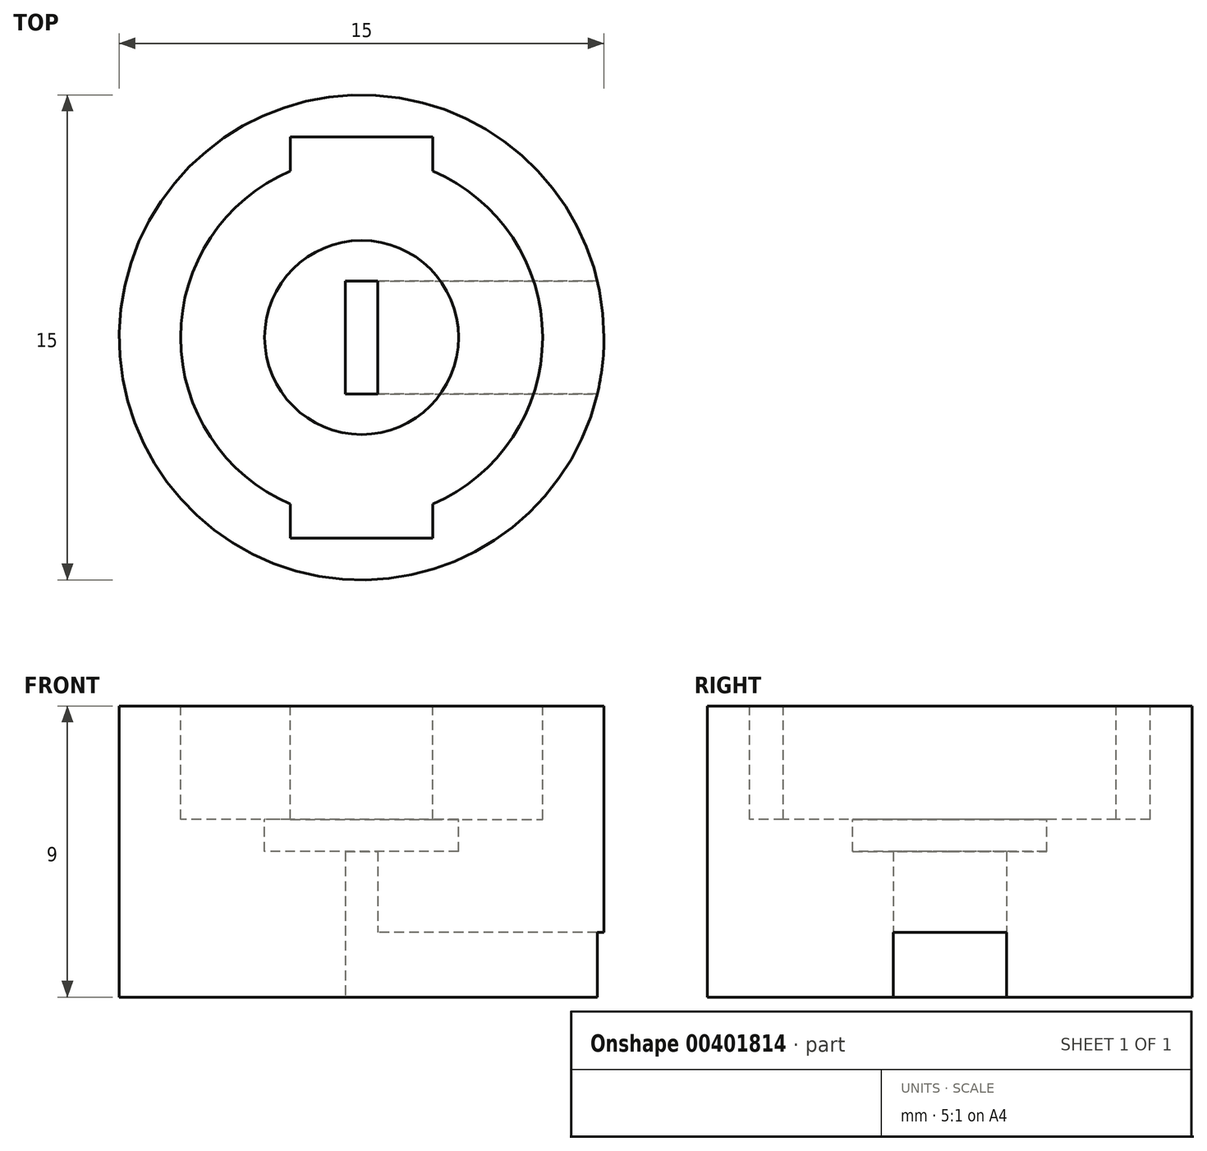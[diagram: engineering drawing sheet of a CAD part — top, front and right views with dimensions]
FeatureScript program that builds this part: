
annotation { "Feature Type Name" : "Feature", "Feature Type Description" : "" }
export const myFeature = defineFeature(function(context is Context, id is Id, definition is map)
    precondition{}
    {
        {
            var Q0;
            Q0=qCreatedBy(makeId("Top.planeOp"),FACE);
            var sketch = newSketch(context, id + "F0", { "sketchPlane" : qUnion([Q0])});
            skCircle(sketch, "E0", {"center": v(0, 0) * mm, "radius": 7.5 * mm});
            skLineSegment(sketch, "E1.bottom", {"start": v(-0.5, 1.75) * mm, "end": v(0.5, 1.75) * mm});
            skLineSegment(sketch, "E1.top", {"start": v(-0.5, -1.75) * mm, "end": v(0.5, -1.75) * mm});
            skLineSegment(sketch, "E1.left", {"start": v(-0.5, 1.75) * mm, "end": v(-0.5, -1.75) * mm});
            skLineSegment(sketch, "E1.right", {"start": v(0.5, 1.75) * mm, "end": v(0.5, -1.75) * mm});
            skPoint(sketch, "E2", {"position": v(-0.5, 0) * mm});
            skPoint(sketch, "E3", {"position": v(0, 1.75) * mm});
            skSolve(sketch);
        }
        {
            var Q0;
            Q0=makeQuery(id+"F0.imprint","IMPRINT",FACE,{"disambiguationData":[TD([[makeQuery(id+"F0.imprint","IMPRINT",EDGE,{"derivedFrom":sQuery(id+"F0.wireOp",EDGE,"E0")}),1.0]])]});
            extrude(context, id + "F1", {"entities" : qUnion([Q0]), "depth" : 9 * mm});
        }
        {
            var Q0;
            Q0=qCreatedBy(makeId("Right.planeOp"),FACE);
            var sketch = newSketch(context, id + "F2", { "sketchPlane" : qUnion([Q0])});
            skLineSegment(sketch, "E4.bottom", {"start": v(-1.75, 0) * mm, "end": v(1.75, 0) * mm});
            skLineSegment(sketch, "E4.top", {"start": v(-1.75, 2) * mm, "end": v(1.75, 2) * mm});
            skLineSegment(sketch, "E4.left", {"start": v(-1.75, 0) * mm, "end": v(-1.75, 2) * mm});
            skLineSegment(sketch, "E4.right", {"start": v(1.75, 0) * mm, "end": v(1.75, 2) * mm});
            skPoint(sketch, "E5", {"position": v(0, 2) * mm});
            skSolve(sketch);
        }
        {
            var Q0;
            Q0 = qSketchRegion(id + "F2", true);
            extrude(context, id + "F3", {"entities" : qUnion([Q0]), "operationType" : NewBodyOperationType.REMOVE, "depth" : 10 * mm});
        }
        {
            var Q0;
            Q0=makeQuery(id+"F1.opExtrude","CAP_FACE",FACE,{"disambiguationData":[OSD([sQuery(id+"F0.wireOp",EDGE,"E0"),sQuery(id+"F0.wireOp",EDGE,"E1.bottom"),sQuery(id+"F0.wireOp",EDGE,"E1.top"),sQuery(id+"F0.wireOp",EDGE,"E1.left"),sQuery(id+"F0.wireOp",EDGE,"E1.right")])],"isStart":false});
            var sketch = newSketch(context, id + "F4", { "sketchPlane" : qUnion([Q0])});
            skLineSegment(sketch, "E6.bottom", {"start": v(-2.2, 6.2) * mm, "end": v(2.2, 6.2) * mm});
            skLineSegment(sketch, "E6.top", {"start": v(-2.2, -6.2) * mm, "end": v(2.2, -6.2) * mm});
            skLineSegment(sketch, "E6.left", {"start": v(-2.2, 6.2) * mm, "end": v(-2.2, -6.2) * mm});
            skLineSegment(sketch, "E6.right", {"start": v(2.2, 6.2) * mm, "end": v(2.2, -6.2) * mm});
            skPoint(sketch, "E7", {"position": v(0, 6.2) * mm});
            skPoint(sketch, "E8", {"position": v(2.2, 0) * mm});
            skCircle(sketch, "E9", {"center": v(0, 0) * mm, "radius": 5.6 * mm});
            skSolve(sketch);
        }
        {
            var Q0;
            {var subQ0=sQuery(id+"F4.wireOp",EDGE,"E9");var subQ1=sQuery(id+"F4.wireOp",EDGE,"E6.left");var subQ2=makeQuery(id+"F4.imprint","INTERSECT",VERTEX,{"disambiguationData":[OD(0.0)],"derivedFrom":[subQ1,subQ0]});Q0=makeQuery(id+"F4.imprint","IMPRINT",FACE,{"disambiguationData":[TD([[makeQuery(id+"F4.imprint","IMPRINT",EDGE,{"disambiguationData":[TD([[subQ2,-1.0]])],"derivedFrom":subQ1}),-1.0]])]});}
            var Q1;
            {var subQ0=sQuery(id+"F4.wireOp",EDGE,"E6.bottom");Q1=makeQuery(id+"F4.imprint","IMPRINT",FACE,{"disambiguationData":[TD([[makeQuery(id+"F4.imprint","IMPRINT",EDGE,{"derivedFrom":subQ0}),-1.0]])]});}
            var Q2;
            Q2=makeQuery(id+"F4.imprint","IMPRINT",FACE,{"disambiguationData":[TD([[makeQuery(id+"F4.imprint","IMPRINT",EDGE,{"derivedFrom":makeQuery(id+"F1.opExtrude","CAP_EDGE",EDGE,{"disambiguationData":[OSD([sQuery(id+"F0.wireOp",EDGE,"E1.bottom")])],"isStart":false})}),1.0]])]});
            var Q3;
            {var subQ0=sQuery(id+"F4.wireOp",EDGE,"E9");var subQ1=sQuery(id+"F4.wireOp",EDGE,"E6.right");var subQ2=makeQuery(id+"F4.imprint","INTERSECT",VERTEX,{"disambiguationData":[OD(0.0)],"derivedFrom":[subQ1,subQ0]});Q3=makeQuery(id+"F4.imprint","IMPRINT",FACE,{"disambiguationData":[TD([[makeQuery(id+"F4.imprint","IMPRINT",EDGE,{"disambiguationData":[TD([[subQ2,-1.0]])],"derivedFrom":subQ1}),1.0]])]});}
            var Q4;
            {var subQ0=sQuery(id+"F4.wireOp",EDGE,"E6.top");Q4=makeQuery(id+"F4.imprint","IMPRINT",FACE,{"disambiguationData":[TD([[makeQuery(id+"F4.imprint","IMPRINT",EDGE,{"derivedFrom":subQ0}),1.0]])]});}
            extrude(context, id + "F5", {"entities" : qUnion([Q0, Q1, Q2, Q3, Q4]), "operationType" : NewBodyOperationType.REMOVE, "oppositeDirection" : true, "depth" : 3.5 * mm});
        }
        {
            var Q0;
            Q0=makeQuery(id+"F5.boolean.opBoolean","COPY",FACE,{"derivedFrom":makeQuery(id+"F5.opExtrude","CAP_FACE",FACE,{"disambiguationData":[OSD([sQuery(id+"F0.wireOp",EDGE,"E1.bottom"),sQuery(id+"F0.wireOp",EDGE,"E1.top"),sQuery(id+"F0.wireOp",EDGE,"E1.left"),sQuery(id+"F0.wireOp",EDGE,"E1.right"),sQuery(id+"F4.wireOp",EDGE,"E6.bottom"),sQuery(id+"F4.wireOp",EDGE,"E6.top"),sQuery(id+"F4.wireOp",EDGE,"E6.left"),sQuery(id+"F4.wireOp",EDGE,"E6.right"),sQuery(id+"F4.wireOp",EDGE,"E9")])],"isStart":false})});
            var sketch = newSketch(context, id + "F6", { "sketchPlane" : qUnion([Q0])});
            skCircle(sketch, "E10", {"center": v(0, 0) * mm, "radius": 3 * mm});
            skSolve(sketch);
        }
        {
            var Q0;
            Q0=makeQuery(id+"F6.imprint","IMPRINT",FACE,{"disambiguationData":[TD([[makeQuery(id+"F6.imprint","IMPRINT",EDGE,{"derivedFrom":sQuery(id+"F6.wireOp",EDGE,"E10")}),1.0]])]});
            extrude(context, id + "F7", {"entities" : qUnion([Q0]), "operationType" : NewBodyOperationType.REMOVE, "oppositeDirection" : true, "depth" : 1 * mm});
        }
    });
